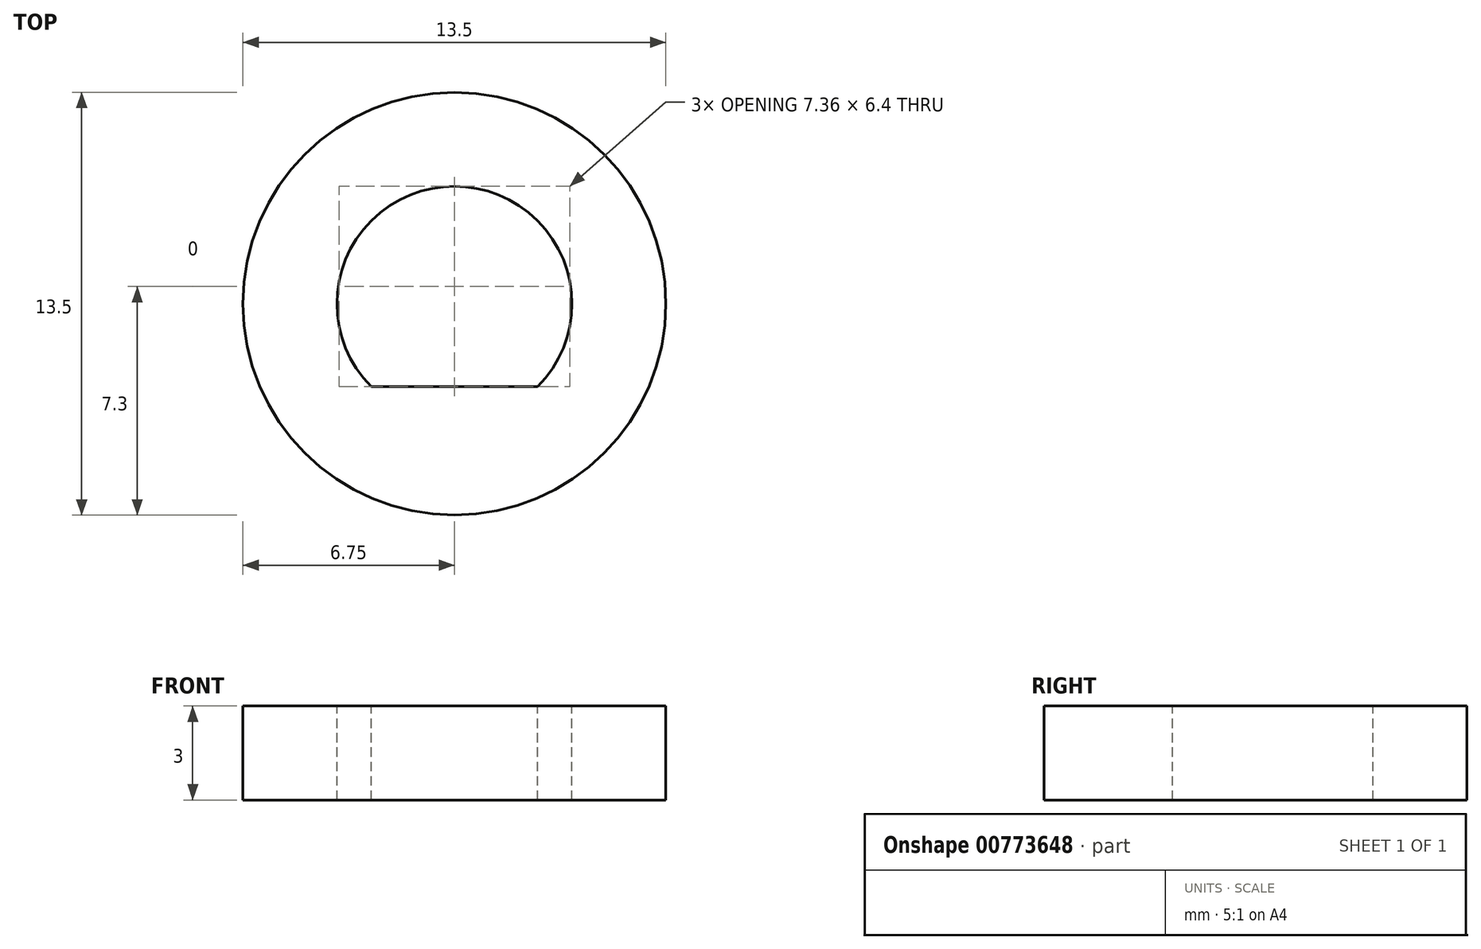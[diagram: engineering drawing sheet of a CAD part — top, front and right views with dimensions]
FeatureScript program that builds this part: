
annotation { "Feature Type Name" : "Feature", "Feature Type Description" : "" }
export const myFeature = defineFeature(function(context is Context, id is Id, definition is map)
    precondition{}
    {
        {
            var Q0;
            Q0=qCreatedBy(makeId("Top.planeOp"),FACE);
            var sketch = newSketch(context, id + "F0", { "sketchPlane" : qUnion([Q0])});
            skCircle(sketch, "E0", {"center": v(0, 0) * mm, "radius": 6.75 * mm});
            skSolve(sketch);
        }
        {
            var Q0;
            Q0=makeQuery(id+"F0.imprint","IMPRINT",FACE,{"disambiguationData":[TD([[makeQuery(id+"F0.imprint","IMPRINT",EDGE,{"derivedFrom":sQuery(id+"F0.wireOp",EDGE,"E0")}),1.0]])]});
            extrude(context, id + "F1", {"entities" : qUnion([Q0]), "depth" : 3 * mm, "offsetDistance" : 25 * mm});
        }
        {
            var Q0;
            Q0=makeQuery(id+"F1.opExtrude","CAP_FACE",FACE,{"disambiguationData":[OSD([sQuery(id+"F0.wireOp",EDGE,"E0")])],"isStart":false});
            var sketch = newSketch(context, id + "F2", { "sketchPlane" : qUnion([Q0])});
            skLineSegment(sketch, "E1.bottom", {"start": v(3.75, 3.75) * mm, "end": v(-3.75, 3.75) * mm});
            skLineSegment(sketch, "E1.top", {"start": v(3.75, -3.75) * mm, "end": v(-3.75, -3.75) * mm});
            skLineSegment(sketch, "E1.left", {"start": v(3.75, 3.75) * mm, "end": v(3.75, -3.75) * mm});
            skLineSegment(sketch, "E1.right", {"start": v(-3.75, 3.75) * mm, "end": v(-3.75, -3.75) * mm});
            skPoint(sketch, "E1.middle", {"position": v(0, 0) * mm});
            skLineSegment(sketch, "E2.bottom", {"start": v(-3.75, -3.75) * mm, "end": v(3.75, -3.75) * mm});
            skLineSegment(sketch, "E2.top", {"start": v(-3.75, -2.65) * mm, "end": v(3.75, -2.65) * mm});
            skLineSegment(sketch, "E2.left", {"start": v(-3.75, -3.75) * mm, "end": v(-3.75, -2.65) * mm});
            skLineSegment(sketch, "E2.right", {"start": v(3.75, -3.75) * mm, "end": v(3.75, -2.65) * mm});
            skCircle(sketch, "E3", {"center": v(0, 0) * mm, "radius": 3.75 * mm});
            skSolve(sketch);
        }
        {
            var Q0;
            {var subQ0=sQuery(id+"F2.wireOp",EDGE,"E3");var subQ2=sQuery(id+"F2.wireOp",EDGE,"E2.top");var subQ3=makeQuery(id+"F2.imprint","INTERSECT",VERTEX,{"disambiguationData":[OD(0.0)],"derivedFrom":[subQ2,subQ0]});Q0=makeQuery(id+"F2.imprint","IMPRINT",FACE,{"disambiguationData":[TD([[makeQuery(id+"F2.imprint","IMPRINT",EDGE,{"disambiguationData":[TD([[subQ3,-1.0]])],"derivedFrom":subQ2}),1.0]])]});}
            extrude(context, id + "F3", {"entities" : qUnion([Q0]), "operationType" : NewBodyOperationType.REMOVE, "oppositeDirection" : true, "depth" : 25 * mm, "offsetDistance" : 25 * mm});
        }
    });
